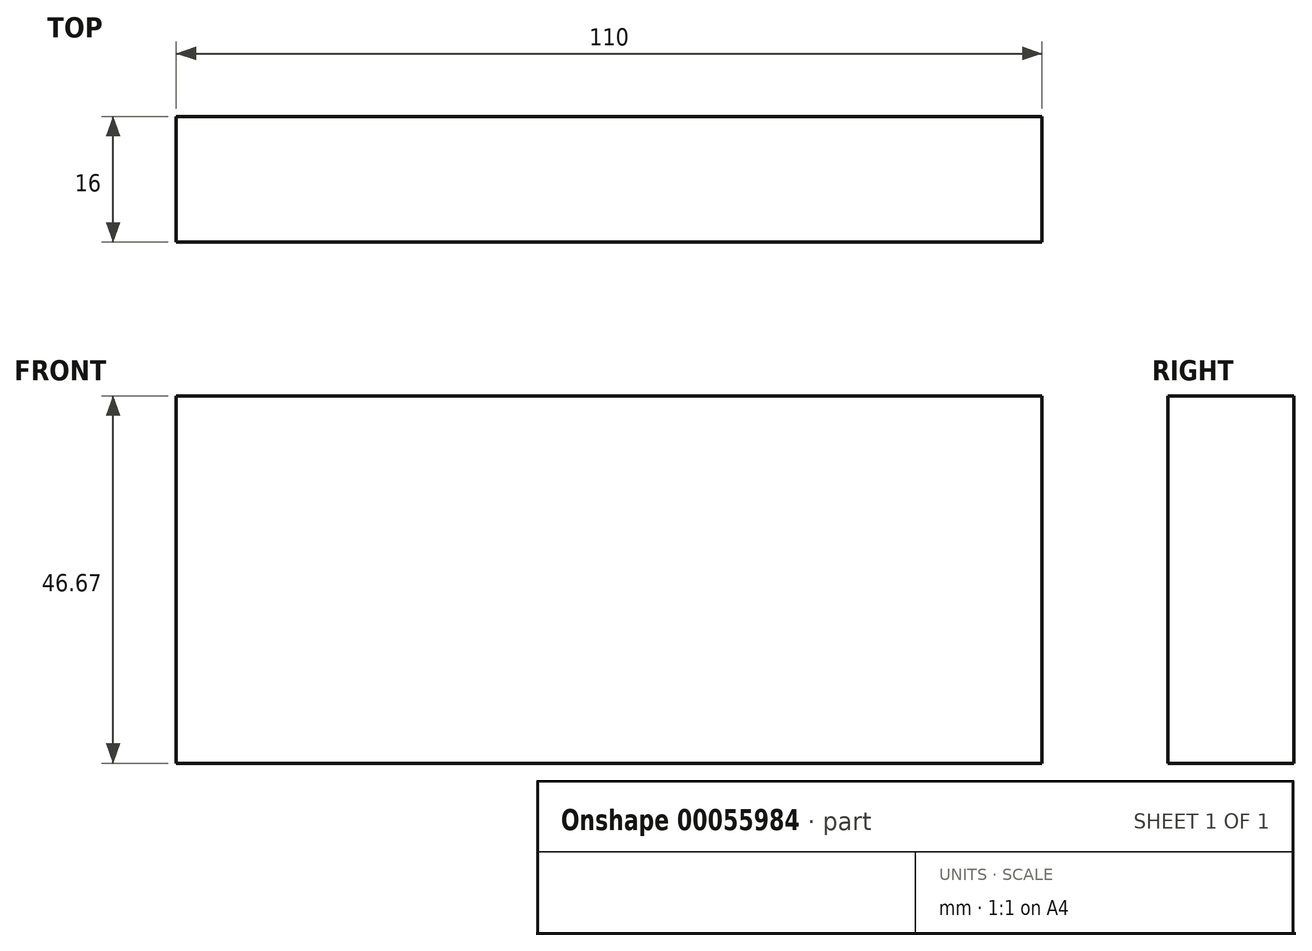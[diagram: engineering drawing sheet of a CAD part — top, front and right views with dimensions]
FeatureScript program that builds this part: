
annotation { "Feature Type Name" : "Feature", "Feature Type Description" : "" }
export const myFeature = defineFeature(function(context is Context, id is Id, definition is map)
    precondition{}
    {
        {
            var Q0;
            Q0=qCreatedBy(makeId("Front.planeOp"),FACE);
            var sketch = newSketch(context, id + "F0", { "sketchPlane" : qUnion([Q0])});
            skLineSegment(sketch, "E0.bottom", {"start": v(0, 0) * mm, "end": v(110, 0) * mm});
            skLineSegment(sketch, "E0.top", {"start": v(0, 46.67) * mm, "end": v(110, 46.67) * mm});
            skLineSegment(sketch, "E0.left", {"start": v(0, 0) * mm, "end": v(0, 46.67) * mm});
            skLineSegment(sketch, "E0.right", {"start": v(110, 0) * mm, "end": v(110, 46.67) * mm});
            skSolve(sketch);
        }
        {
            var Q0;
            Q0=makeQuery(id+"F0.imprint","IMPRINT",FACE,{"disambiguationData":[TD([[makeQuery(id+"F0.imprint","IMPRINT",EDGE,{"derivedFrom":sQuery(id+"F0.wireOp",EDGE,"E0.bottom")}),1.0]])]});
            extrude(context, id + "F1", {"entities" : qUnion([Q0]), "depth" : 16 * mm});
        }
    });
